# Revit family: Lixil-Grohe-Listra-Level_Handles-Lav-106257_0 new
name_source: partatom
category: Plumbing Fixtures
units: mm (PartAtom-declared; Revit-internal decimal feet)

## family parameters
Cut with Voids When Loaded = No
Enable Cutting in Views = Yes
Host = Face
Maintain Annotation Orientation = No
OmniClass Number = 23.45.55.17
OmniClass Title = Mixing Faucets
Part Type = Normal
Room Calculation Point = No
Round Connector Dimension = Use Diameter
Shared = No

## types (2) — shared parameters
Assembly Code = D2010400
Brand = Grohe
CW Connection = Yes
Collection = Listra
Default Elevation = 0"
Depth = 2 1/4"
Description = Listra Level Handles, Lav
Finish = Metal - Grohe - Chrome
HW Connection = Yes
Height = 2 7/8"
Keynote = 22 40 00
Manufacturer = LIXIL
Model = 106257_0
Product Documentation Link = https://www.grohe.us
Product Name = Listra Level Handles, Lav
Product Page URL = https://www.grohe.us
URL = https://www.grohe.us
Vent Connection = No
Version = 2023 - v1.0a
Warranty URL = https://www.grohe.us
Waste Connection = No
Width = 8 15/16"

## per-type parameters (varying)
| type | Left | Right |
| Listra Lever Handles - Lav - Left | Yes | No |
| Listra Lever Handles - Lav - Right | No | Yes |

## geometry (parser evidence)
native form markers: Sweep x1
no freeform markers — native parametric forms only
